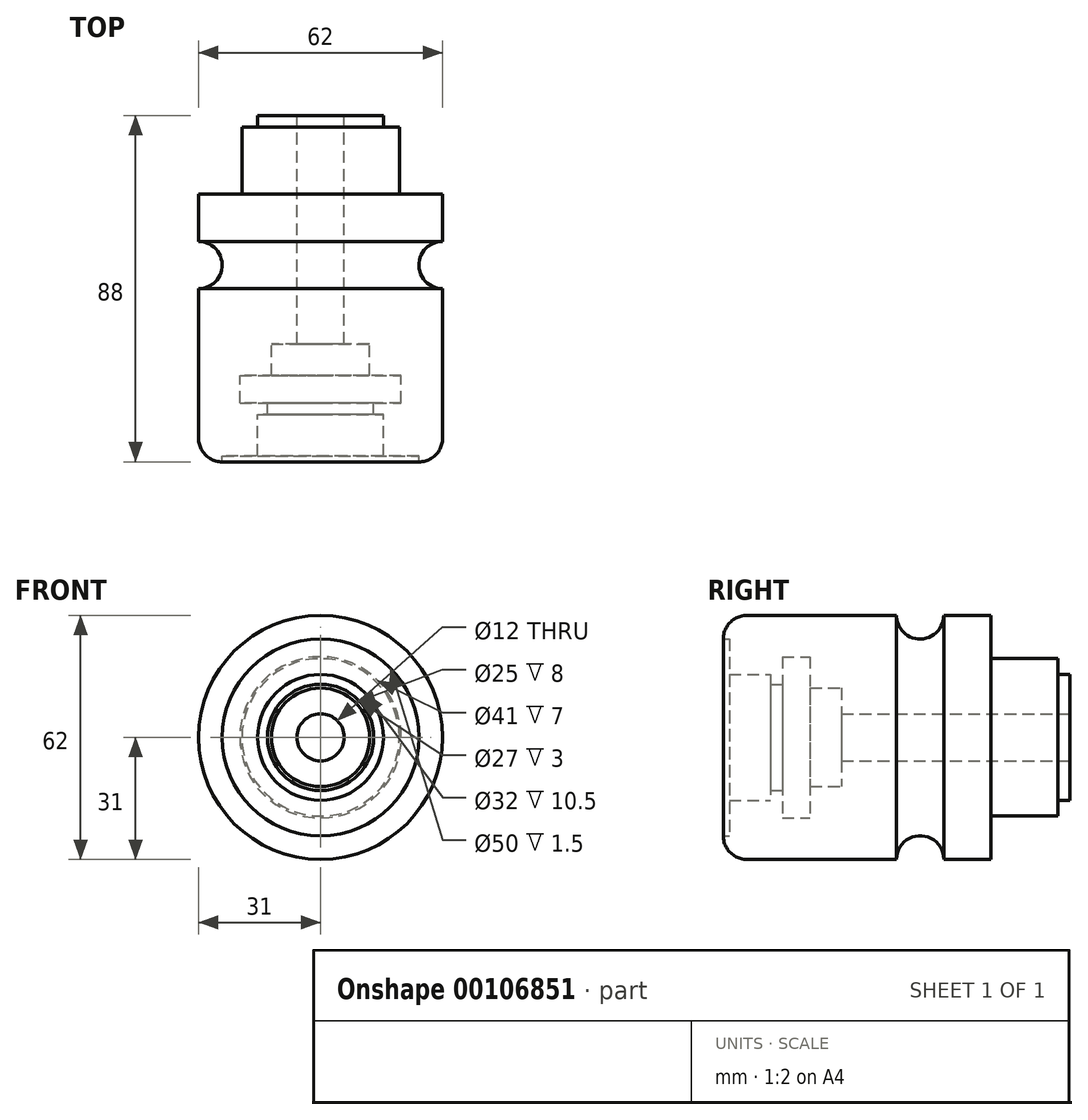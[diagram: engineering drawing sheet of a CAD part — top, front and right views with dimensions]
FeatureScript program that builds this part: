
annotation { "Feature Type Name" : "Feature", "Feature Type Description" : "" }
export const myFeature = defineFeature(function(context is Context, id is Id, definition is map)
    precondition{}
    {
        {
            var Q0;
            Q0=qCreatedBy(makeId("Right.planeOp"),FACE);
            var sketch = newSketch(context, id + "F0", { "sketchPlane" : qUnion([Q0])});
            skLineSegment(sketch, "E0", {"start": v(0, 0) * mm, "end": v(68, 0) * mm});
            skLineSegment(sketch, "E1", {"start": v(68, 0) * mm, "end": v(68, 31) * mm});
            skLineSegment(sketch, "E2", {"start": v(68, 31) * mm, "end": v(56, 31) * mm});
            skLineSegment(sketch, "E3", {"start": v(0, 0) * mm, "end": v(0, 25) * mm});
            skLineSegment(sketch, "E4", {"start": v(6, 31) * mm, "end": v(44, 31) * mm});
            skLineSegment(sketch, "E5", {"start": v(68, 20) * mm, "end": v(85, 20) * mm});
            skLineSegment(sketch, "E6", {"start": v(85, 20) * mm, "end": v(85, 0) * mm});
            skLineSegment(sketch, "E7", {"start": v(85, 0) * mm, "end": v(68, 0) * mm});
            skLineSegment(sketch, "E8", {"start": v(85, 16) * mm, "end": v(88, 16) * mm});
            skLineSegment(sketch, "E9", {"start": v(88, 16) * mm, "end": v(88, 0) * mm});
            skLineSegment(sketch, "E10", {"start": v(88, 0) * mm, "end": v(85, 0) * mm});
            skArc(sketch, "E11", {"start": v(44, 31) * mm, "mid": v(50, 25) * mm, "end": v(56, 31) * mm});
            skPoint(sketch, "E12.visualSharp", {"position": v(0, 31) * mm});
            skArc(sketch, "E12.filletArc", {"start": v(6, 31) * mm, "mid": v(1.76, 29.24) * mm, "end": v(0, 25) * mm});
            skLineSegment(sketch, "E13", {"start": v(0, 0) * mm, "end": v(128.72, 0) * mm, "construction": true});
            skSolve(sketch);
        }
        {
            var Q0;
            Q0 = qSketchRegion(id + "F0", true);
            var Q1;
            Q1=sQuery(id+"F0.wireOp",EDGE,"E13");
            revolve(context, id + "F1", {"entities" : qUnion([Q0]), "axis" : qUnion([Q1]), "revolveType" : RevolveType.FULL});
        }
        {
            var Q0;
            Q0=qCreatedBy(makeId("Right.planeOp"),FACE);
            var sketch = newSketch(context, id + "F2", { "sketchPlane" : qUnion([Q0])});
            skLineSegment(sketch, "E14", {"start": v(0, 0) * mm, "end": v(96.62, 0) * mm, "construction": true});
            skLineSegment(sketch, "E15", {"start": v(0, 0) * mm, "end": v(0, 25) * mm});
            skLineSegment(sketch, "E16", {"start": v(0, 25) * mm, "end": v(1.5, 25) * mm});
            skLineSegment(sketch, "E17", {"start": v(1.5, 25) * mm, "end": v(1.5, 0) * mm});
            skLineSegment(sketch, "E18", {"start": v(1.5, 0) * mm, "end": v(0, 0) * mm});
            skLineSegment(sketch, "E19", {"start": v(1.5, 16) * mm, "end": v(12, 16) * mm});
            skLineSegment(sketch, "E20", {"start": v(12, 16) * mm, "end": v(12, 0) * mm});
            skLineSegment(sketch, "E21", {"start": v(12, 0) * mm, "end": v(1.5, 0) * mm});
            skLineSegment(sketch, "E22", {"start": v(15, 0) * mm, "end": v(12, 0) * mm});
            skLineSegment(sketch, "E23", {"start": v(15, 20.5) * mm, "end": v(22, 20.5) * mm});
            skLineSegment(sketch, "E24", {"start": v(22, 20.5) * mm, "end": v(22, 0) * mm});
            skLineSegment(sketch, "E25", {"start": v(22, 0) * mm, "end": v(15, 0) * mm});
            skLineSegment(sketch, "E26", {"start": v(22, 12.5) * mm, "end": v(30, 12.5) * mm});
            skLineSegment(sketch, "E27", {"start": v(30, 12.5) * mm, "end": v(30, 0) * mm});
            skLineSegment(sketch, "E28", {"start": v(30, 0) * mm, "end": v(22, 0) * mm});
            skLineSegment(sketch, "E29", {"start": v(30, 6) * mm, "end": v(88, 6) * mm});
            skLineSegment(sketch, "E30", {"start": v(88, 6) * mm, "end": v(88, 0) * mm});
            skLineSegment(sketch, "E31", {"start": v(88, 0) * mm, "end": v(30, 0) * mm});
            skLineSegment(sketch, "E32", {"start": v(15, 20.5) * mm, "end": v(15, 0) * mm});
            skLineSegment(sketch, "E33", {"start": v(15, 13.5) * mm, "end": v(12, 13.5) * mm});
            skLineSegment(sketch, "E34", {"start": v(12, 0) * mm, "end": v(15, 0) * mm});
            skLineSegment(sketch, "E35", {"start": v(15, 0) * mm, "end": v(22, 0) * mm});
            skLineSegment(sketch, "E36", {"start": v(22, 0) * mm, "end": v(30, 0) * mm});
            skLineSegment(sketch, "E37", {"start": v(30, 0) * mm, "end": v(88, 0) * mm});
            skLineSegment(sketch, "E38", {"start": v(12, 13.5) * mm, "end": v(12, 0) * mm});
            skLineSegment(sketch, "E39", {"start": v(15, 13.5) * mm, "end": v(15, 0) * mm});
            skSolve(sketch);
        }
        {
            var Q0;
            Q0 = qSketchRegion(id + "F2", true);
            var Q1;
            Q1=sQuery(id+"F2.wireOp",EDGE,"E14");
            revolve(context, id + "F3", {"operationType" : NewBodyOperationType.REMOVE, "entities" : qUnion([Q0]), "axis" : qUnion([Q1]), "revolveType" : RevolveType.FULL, "oppositeDirection" : true});
        }
    });
